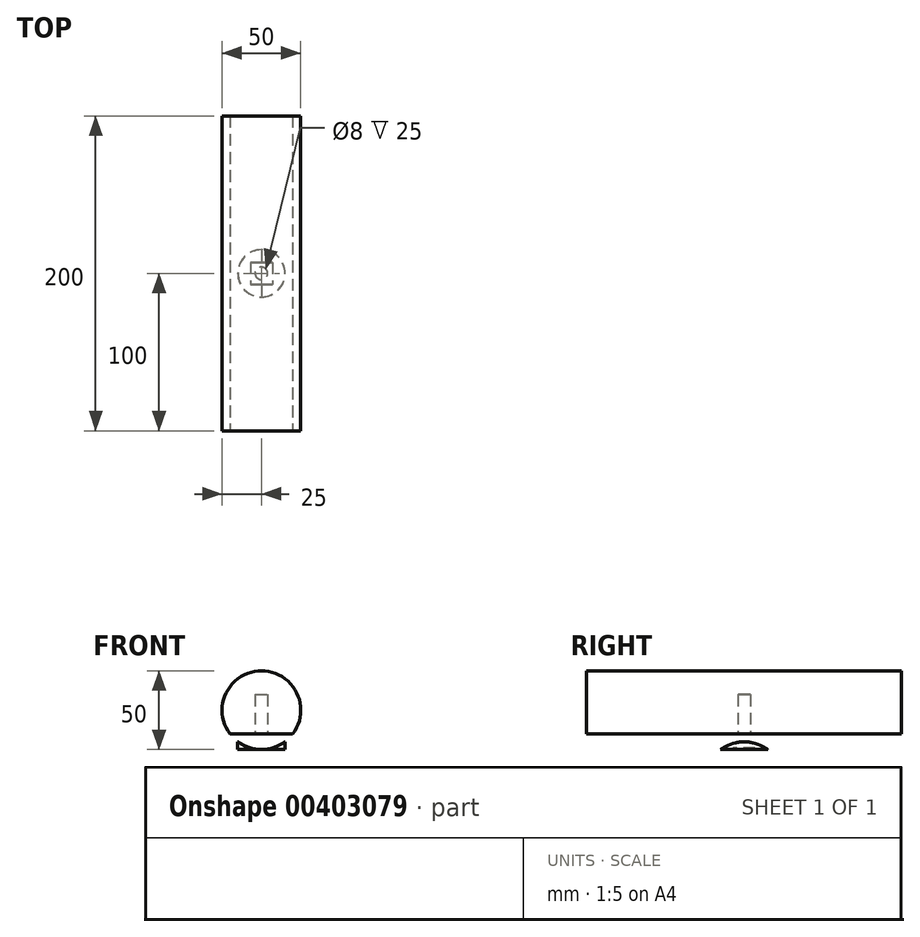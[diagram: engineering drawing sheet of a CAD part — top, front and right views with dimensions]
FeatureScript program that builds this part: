
annotation { "Feature Type Name" : "Feature", "Feature Type Description" : "" }
export const myFeature = defineFeature(function(context is Context, id is Id, definition is map)
    precondition{}
    {
        {
            var Q0;
            Q0=qCreatedBy(makeId("Top.planeOp"),FACE);
            var sketch = newSketch(context, id + "F0", { "sketchPlane" : qUnion([Q0])});
            skCircle(sketch, "E0", {"center": v(0, 0) * mm, "radius": 15 * mm});
            skSolve(sketch);
        }
        {
            var Q0;
            Q0=makeQuery(id+"F0.imprint","IMPRINT",FACE,{"disambiguationData":[TD([[makeQuery(id+"F0.imprint","IMPRINT",EDGE,{"derivedFrom":sQuery(id+"F0.wireOp",EDGE,"E0")}),1.0]])]});
            extrude(context, id + "F1", {"entities" : qUnion([Q0]), "depth" : 10 * mm});
        }
        {
            var Q0;
            Q0=qCreatedBy(makeId("Front.planeOp"),FACE);
            var sketch = newSketch(context, id + "F2", { "sketchPlane" : qUnion([Q0])});
            skPoint(sketch, "E1", {"position": v(0, 25) * mm});
            skCircle(sketch, "E2", {"center": v(0, 25) * mm, "radius": 25 * mm});
            skLineSegment(sketch, "E3.bottom", {"start": v(-35.46, 56.3) * mm, "end": v(43.95, 56.3) * mm});
            skLineSegment(sketch, "E3.top", {"start": v(-35.46, 9.9) * mm, "end": v(43.95, 9.9) * mm});
            skLineSegment(sketch, "E3.left", {"start": v(-35.46, 56.3) * mm, "end": v(-35.46, 9.9) * mm});
            skLineSegment(sketch, "E3.right", {"start": v(43.95, 56.3) * mm, "end": v(43.95, 9.9) * mm});
            skSolve(sketch);
        }
        {
            var Q0;
            Q0=makeQuery(id+"F2.imprint","IMPRINT",FACE,{"disambiguationData":[TD([[makeQuery(id+"F2.imprint","IMPRINT",EDGE,{"derivedFrom":sQuery(id+"F2.wireOp",EDGE,"E2")}),1.0]])]});
            extrude(context, id + "F3", {"entities" : qUnion([Q0]), "operationType" : NewBodyOperationType.ADD, "depth" : 100 * mm, "hasSecondDirection" : true, "secondDirectionOppositeDirection" : true, "secondDirectionDepth" : 100 * mm});
        }
        {
            var Q0;
            Q0=makeQuery(id+"F2.imprint","IMPRINT",FACE,{"disambiguationData":[TD([[makeQuery(id+"F2.imprint","IMPRINT",EDGE,{"derivedFrom":sQuery(id+"F2.wireOp",EDGE,"E3.bottom")}),-1.0]])]});
            var Q1;
            {var subQ0=sQuery(id+"F2.wireOp",EDGE,"E3.top");var subQ1=sQuery(id+"F2.wireOp",EDGE,"E2");var subQ2=makeQuery(id+"F2.imprint","INTERSECT",VERTEX,{"disambiguationData":[OD(0.0)],"derivedFrom":[subQ1,subQ0]});Q1=makeQuery(id+"F2.imprint","IMPRINT",FACE,{"disambiguationData":[TD([[makeQuery(id+"F2.imprint","IMPRINT",EDGE,{"disambiguationData":[TD([[subQ2,1.0]])],"derivedFrom":subQ1}),1.0]])]});}
            extrude(context, id + "F4", {"entities" : qUnion([Q0, Q1]), "operationType" : NewBodyOperationType.REMOVE, "oppositeDirection" : true, "depth" : 100 * mm, "hasSecondDirection" : true, "secondDirectionOppositeDirection" : false, "secondDirectionDepth" : 100 * mm});
        }
        {
            var Q0;
            Q0=makeQuery(id+"F4.boolean.opBoolean","COPY",FACE,{"derivedFrom":makeQuery(id+"F4.opExtrude","SWEPT_FACE",FACE,{"disambiguationData":[OSD([sQuery(id+"F2.wireOp",EDGE,"E3.top")])]})});
            var sketch = newSketch(context, id + "F5", { "sketchPlane" : qUnion([Q0])});
            skCircle(sketch, "E4", {"center": v(0, 0) * mm, "radius": 4 * mm});
            skSolve(sketch);
        }
        {
            var Q0;
            Q0=makeQuery(id+"F5.imprint","IMPRINT",FACE,{"disambiguationData":[TD([[makeQuery(id+"F5.imprint","IMPRINT",EDGE,{"derivedFrom":sQuery(id+"F5.wireOp",EDGE,"E4")}),1.0]])]});
            extrude(context, id + "F6", {"entities" : qUnion([Q0]), "operationType" : NewBodyOperationType.REMOVE, "oppositeDirection" : true, "depth" : 25 * mm});
        }
        {
            var Q0;
            Q0=makeQuery(id+"F1.opExtrude","CAP_FACE",FACE,{"disambiguationData":[OSD([sQuery(id+"F0.wireOp",EDGE,"E0")])],"isStart":true});
            var sketch = newSketch(context, id + "F7", { "sketchPlane" : qUnion([Q0])});
            skLineSegment(sketch, "E5.bottom", {"start": v(7, -7) * mm, "end": v(-7, -7) * mm});
            skLineSegment(sketch, "E5.top", {"start": v(7, 7) * mm, "end": v(-7, 7) * mm});
            skLineSegment(sketch, "E5.left", {"start": v(7, -7) * mm, "end": v(7, 7) * mm});
            skLineSegment(sketch, "E5.right", {"start": v(-7, -7) * mm, "end": v(-7, 7) * mm});
            skPoint(sketch, "E5.middle", {"position": v(0, 0) * mm});
            skSolve(sketch);
        }
        {
            var Q0;
            Q0=makeQuery(id+"F7.imprint","IMPRINT",FACE,{"disambiguationData":[TD([[makeQuery(id+"F7.imprint","IMPRINT",EDGE,{"derivedFrom":sQuery(id+"F7.wireOp",EDGE,"E5.bottom")}),-1.0]])]});
            extrude(context, id + "F8", {"entities" : qUnion([Q0]), "operationType" : NewBodyOperationType.REMOVE, "oppositeDirection" : true, "depth" : 5 * mm});
        }
    });
